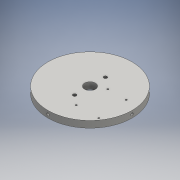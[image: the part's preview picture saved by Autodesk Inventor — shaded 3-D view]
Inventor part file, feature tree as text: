
AUTODESK INVENTOR PART (.ipt)
format: ipt  version: 2016 (Build 200138000, 138)  size: 164,864 bytes
history: native  units: mm
features: extrude x7, thread x6, sketch x6, other x5
ambient origin geometry x8: Origin, YZ Plane, XZ Plane, XY Plane, X Axis, Y Axis, Z Axis, Center Point
bodies: Body1 (feature_tree)
feature tree (24):
  other  "ソリッド1"
  extrude  "押し出し1"  Depth=101.0mm
  other  "作業平面1"
  other  "作業平面2"
  other  "作業平面3"
  other  "作業平面4"
  extrude  "押し出し2"  Depth=8.0mm TaperAngle=0.0deg
  extrude  "押し出し3"  Depth=50.5mm
  extrude  "押し出し4"  Depth=4.0mm
  extrude  "押し出し5"  Depth=3.0mm
  thread  "ねじ1"
  thread  "ねじ2"
  thread  "ねじ3"
  thread  "ねじ4"
  extrude  "押し出し7"  Depth=5.0mm TaperAngle=0.0deg
  thread  "ねじ7"
  thread  "ねじ8"
  sketch  "スケッチ9"
  extrude  "押し出し11"  Depth=4.0mm
  sketch  "スケッチ1"
  sketch  "スケッチ2"
  sketch  "スケッチ3"
  sketch  "スケッチ4"
  sketch  "スケッチ5"
